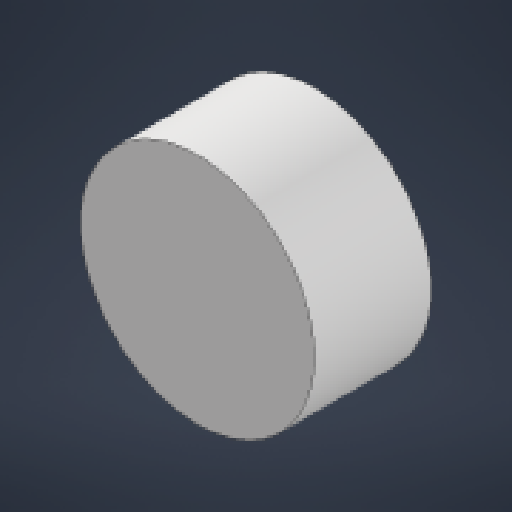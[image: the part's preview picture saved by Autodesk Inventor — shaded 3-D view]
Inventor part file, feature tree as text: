
AUTODESK INVENTOR PART (.ipt)
format: ipt  version: 2023 (Build 270158000, 158)  size: 115,200 bytes
history: native  units: in
note: dims shown in document units (in); Inventor stores cm internally (conversion verified against a paired STEP export)
features: extrude x1, sketch x1
ambient origin geometry x8: Origin, YZ Plane, XZ Plane, XY Plane, X Axis, Y Axis, Z Axis, Center Point
bodies: Solid1 (feature_tree)
feature tree (2):
  extrude  "Extrusion1"  Depth=1.1811in TaperAngle=0.0deg
  sketch  "Sketch1"  dims[d0=2.3622in d1=1.1811in d2=0.0in]
